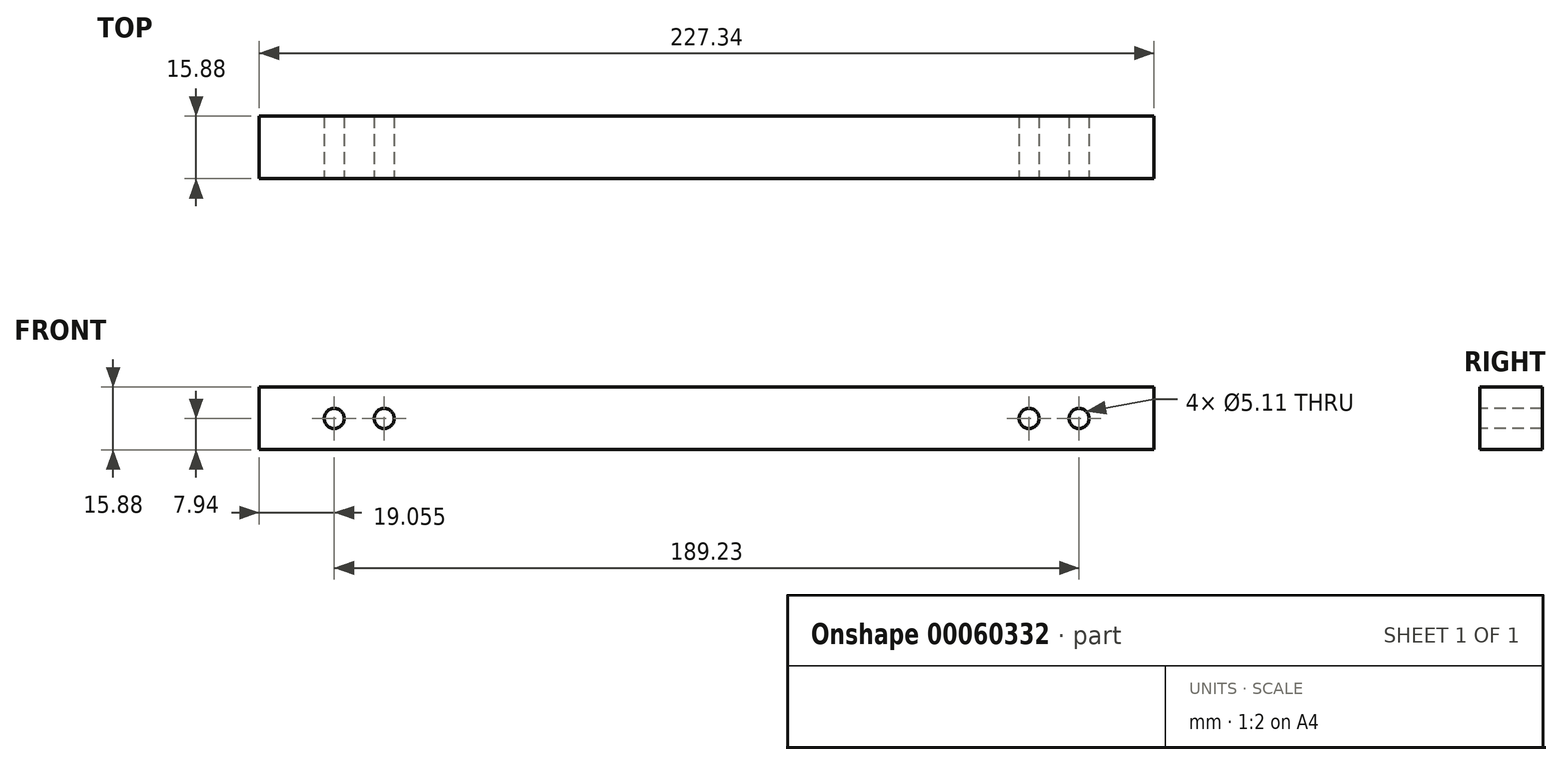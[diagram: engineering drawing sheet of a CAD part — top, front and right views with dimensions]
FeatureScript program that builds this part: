
annotation { "Feature Type Name" : "Feature", "Feature Type Description" : "" }
export const myFeature = defineFeature(function(context is Context, id is Id, definition is map)
    precondition{}
    {
        {
            var Q0;
            Q0=qCreatedBy(makeId("Front.planeOp"),FACE);
            var sketch = newSketch(context, id + "F0", { "sketchPlane" : qUnion([Q0])});
            skLineSegment(sketch, "E0.rect.bottom", {"start": v(113.66, -7.94) * mm, "end": v(-113.67, -7.94) * mm});
            skLineSegment(sketch, "E0.rect.top", {"start": v(113.67, 7.94) * mm, "end": v(-113.67, 7.94) * mm});
            skLineSegment(sketch, "E0.rect.left", {"start": v(113.67, -7.94) * mm, "end": v(113.67, 7.94) * mm});
            skLineSegment(sketch, "E0.rect.right", {"start": v(-113.67, -7.94) * mm, "end": v(-113.67, 7.94) * mm});
            skPoint(sketch, "E0.rect.middle", {"position": v(0, 0) * mm});
            skSolve(sketch);
        }
        {
            var Q0;
            Q0 = qSketchRegion(id + "F0", true);
            extrude(context, id + "F1", {"entities" : qUnion([Q0]), "depth" : 15.88 * mm});
        }
        {
            var Q0;
            Q0=makeQuery(id+"F1.opExtrude","CAP_FACE",FACE,{"disambiguationData":[OSD([sQuery(id+"F0.wireOp",EDGE,"E0.rect.bottom"),sQuery(id+"F0.wireOp",EDGE,"E0.rect.top"),sQuery(id+"F0.wireOp",EDGE,"E0.rect.left"),sQuery(id+"F0.wireOp",EDGE,"E0.rect.right")])],"isStart":false});
            var sketch = newSketch(context, id + "F2", { "sketchPlane" : qUnion([Q0])});
            skPoint(sketch, "E1", {"position": v(-94.62, 0) * mm});
            skPoint(sketch, "E2", {"position": v(-81.92, 0) * mm});
            skPoint(sketch, "E3", {"position": v(94.62, 0) * mm});
            skPoint(sketch, "E4", {"position": v(81.92, 0) * mm});
            skSolve(sketch);
        }
        {
            var Q0;
            Q0=sQuery(id+"F2.wireOp",VERTEX,"E1");
            var Q1;
            Q1=sQuery(id+"F2.wireOp",VERTEX,"E2");
            var Q2;
            Q2=sQuery(id+"F2.wireOp",VERTEX,"E4");
            var Q3;
            Q3=sQuery(id+"F2.wireOp",VERTEX,"E3");
            var Q4;
            Q4=makeQuery(id+"F1.opExtrude","SWEPT_BODY",BODY,{"disambiguationData":[OSD([sQuery(id+"F0.wireOp",EDGE,"E0.rect.bottom"),sQuery(id+"F0.wireOp",EDGE,"E0.rect.top"),sQuery(id+"F0.wireOp",EDGE,"E0.rect.left"),sQuery(id+"F0.wireOp",EDGE,"E0.rect.right")])]});
            hole(context, id + "F3", {"style" : HoleStyle.SIMPLE, "holeDiameter" : 5.1 * mm, "endStyle" : HoleEndStyle.THROUGH, "standardTappedOrClearance" : lookupTablePath({ "standard" : "ANSI", "engagement" : "75%", "pitch" : "20 tpi", "size" : "1/4", "type" : "Tapped" }), "standardBlindInLast" : lookupTablePath({ "standard" : "ANSI", "fit" : "Free", "engagement" : "75%", "pitch" : "20 tpi", "size" : "1/4", "type" : "Clearance & tapped" }), "locations" : qUnion([Q0, Q1, Q2, Q3]), "scope" : qUnion([Q4]), "majorDiameter" : 6.35 * mm, "showTappedDepth" : true, "isTappedThrough" : true, "tappedDepth" : 12.7 * mm, "tapClearance" : 3});
        }
    });
